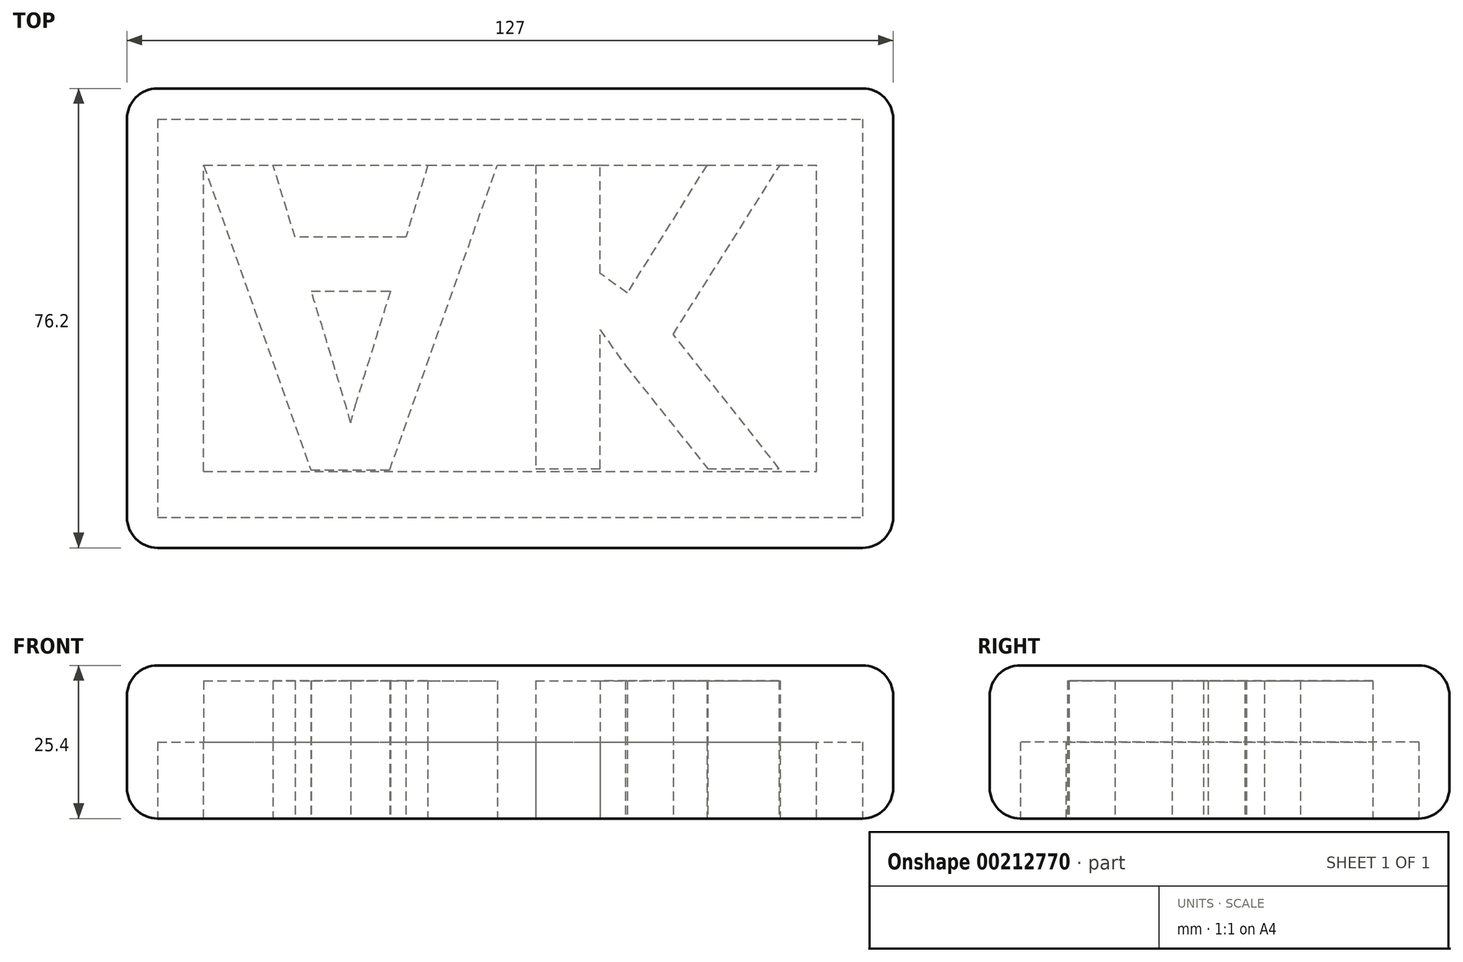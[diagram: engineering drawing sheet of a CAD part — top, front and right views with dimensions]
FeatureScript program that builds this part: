
annotation { "Feature Type Name" : "Feature", "Feature Type Description" : "" }
export const myFeature = defineFeature(function(context is Context, id is Id, definition is map)
    precondition{}
    {
        {
            var Q0;
            Q0=qCreatedBy(makeId("Top.planeOp"),FACE);
            var sketch = newSketch(context, id + "F0", { "sketchPlane" : qUnion([Q0])});
            skLineSegment(sketch, "E0.bottom", {"start": v(-63.5, 38.1) * mm, "end": v(63.5, 38.1) * mm});
            skLineSegment(sketch, "E0.top", {"start": v(-63.5, -38.1) * mm, "end": v(63.5, -38.1) * mm});
            skLineSegment(sketch, "E0.left", {"start": v(-63.5, 38.1) * mm, "end": v(-63.5, -38.1) * mm});
            skLineSegment(sketch, "E0.right", {"start": v(63.5, 38.1) * mm, "end": v(63.5, -38.1) * mm});
            skPoint(sketch, "E0.middle", {"position": v(0, 0) * mm});
            skSolve(sketch);
        }
        {
            var Q0;
            Q0=makeQuery(id+"F0.imprint","IMPRINT",FACE,{"disambiguationData":[TD([[makeQuery(id+"F0.imprint","IMPRINT",EDGE,{"derivedFrom":sQuery(id+"F0.wireOp",EDGE,"E0.bottom")}),-1.0]])]});
            extrude(context, id + "F1", {"entities" : qUnion([Q0]), "depth" : 25.4 * mm});
        }
        {
            var Q0;
            Q0=makeQuery(id+"F1.opExtrude","SWEPT_EDGE",EDGE,{"disambiguationData":[OSD([sQuery(id+"F0.wireOp",EDGE,"E0.bottom"),sQuery(id+"F0.wireOp",EDGE,"E0.left")])]});
            var Q1;
            Q1=makeQuery(id+"F1.opExtrude","CAP_EDGE",EDGE,{"disambiguationData":[OSD([sQuery(id+"F0.wireOp",EDGE,"E0.left")])],"isStart":false});
            var Q2;
            Q2=makeQuery(id+"F1.opExtrude","CAP_EDGE",EDGE,{"disambiguationData":[OSD([sQuery(id+"F0.wireOp",EDGE,"E0.bottom")])],"isStart":false});
            var Q3;
            Q3=makeQuery(id+"F1.opExtrude","CAP_EDGE",EDGE,{"disambiguationData":[OSD([sQuery(id+"F0.wireOp",EDGE,"E0.top")])],"isStart":false});
            var Q4;
            Q4=makeQuery(id+"F1.opExtrude","SWEPT_EDGE",EDGE,{"disambiguationData":[OSD([sQuery(id+"F0.wireOp",EDGE,"E0.top"),sQuery(id+"F0.wireOp",EDGE,"E0.left")])]});
            var Q5;
            Q5=makeQuery(id+"F1.opExtrude","CAP_EDGE",EDGE,{"disambiguationData":[OSD([sQuery(id+"F0.wireOp",EDGE,"E0.left")])],"isStart":true});
            var Q6;
            Q6=makeQuery(id+"F1.opExtrude","CAP_EDGE",EDGE,{"disambiguationData":[OSD([sQuery(id+"F0.wireOp",EDGE,"E0.bottom")])],"isStart":true});
            var Q7;
            Q7=makeQuery(id+"F1.opExtrude","SWEPT_EDGE",EDGE,{"disambiguationData":[OSD([sQuery(id+"F0.wireOp",EDGE,"E0.bottom"),sQuery(id+"F0.wireOp",EDGE,"E0.right")])]});
            var Q8;
            Q8=makeQuery(id+"F1.opExtrude","CAP_EDGE",EDGE,{"disambiguationData":[OSD([sQuery(id+"F0.wireOp",EDGE,"E0.right")])],"isStart":false});
            var Q9;
            Q9=makeQuery(id+"F1.opExtrude","CAP_EDGE",EDGE,{"disambiguationData":[OSD([sQuery(id+"F0.wireOp",EDGE,"E0.right")])],"isStart":true});
            var Q10;
            Q10=makeQuery(id+"F1.opExtrude","CAP_EDGE",EDGE,{"disambiguationData":[OSD([sQuery(id+"F0.wireOp",EDGE,"E0.top")])],"isStart":true});
            var Q11;
            Q11=makeQuery(id+"F1.opExtrude","SWEPT_EDGE",EDGE,{"disambiguationData":[OSD([sQuery(id+"F0.wireOp",EDGE,"E0.top"),sQuery(id+"F0.wireOp",EDGE,"E0.right")])]});
            fillet(context, id + "F2", {"entities" : qUnion([Q0, Q1, Q2, Q3, Q4, Q5, Q6, Q7, Q8, Q9, Q10, Q11]), "radius" : 5.08 * mm, "tangentPropagation" : true, "allowEdgeOverflow" : false});
        }
        {
            var Q0;
            Q0=makeQuery(id+"F1.opExtrude","CAP_FACE",FACE,{"disambiguationData":[OSD([sQuery(id+"F0.wireOp",EDGE,"E0.bottom"),sQuery(id+"F0.wireOp",EDGE,"E0.top"),sQuery(id+"F0.wireOp",EDGE,"E0.left"),sQuery(id+"F0.wireOp",EDGE,"E0.right")])],"isStart":true});
            extrude(context, id + "F3", {"entities" : qUnion([Q0]), "operationType" : NewBodyOperationType.REMOVE, "oppositeDirection" : true, "depth" : 12.7 * mm});
        }
        {
            var Q0;
            Q0=makeQuery(id+"F3.boolean.opBoolean","COPY",FACE,{"derivedFrom":makeQuery(id+"F3.opExtrude","CAP_FACE",FACE,{"disambiguationData":[OSD([sQuery(id+"F0.wireOp",EDGE,"E0.bottom"),sQuery(id+"F0.wireOp",EDGE,"E0.top"),sQuery(id+"F0.wireOp",EDGE,"E0.left"),sQuery(id+"F0.wireOp",EDGE,"E0.right")])],"isStart":false})});
            var sketch = newSketch(context, id + "F4", { "sketchPlane" : qUnion([Q0])});
            skLineSegment(sketch, "E1.bottom", {"start": v(-50.8, 25.4) * mm, "end": v(50.8, 25.4) * mm});
            skLineSegment(sketch, "E1.top", {"start": v(-50.8, -25.4) * mm, "end": v(50.8, -25.4) * mm});
            skLineSegment(sketch, "E1.left", {"start": v(-50.8, 25.4) * mm, "end": v(-50.8, -25.4) * mm});
            skLineSegment(sketch, "E1.right", {"start": v(50.8, 25.4) * mm, "end": v(50.8, -25.4) * mm});
            skPoint(sketch, "E1.middle", {"position": v(0, 0) * mm});
            skSolve(sketch);
        }
        {
            var Q0;
            Q0=makeQuery(id+"F4.imprint","IMPRINT",FACE,{"disambiguationData":[TD([[makeQuery(id+"F4.imprint","IMPRINT",EDGE,{"derivedFrom":sQuery(id+"F4.wireOp",EDGE,"E1.bottom")}),-1.0]])]});
            extrude(context, id + "F5", {"entities" : qUnion([Q0]), "operationType" : NewBodyOperationType.ADD, "depth" : 12.7 * mm});
        }
        {
            var Q0;
            Q0=makeQuery(id+"F5.opExtrude","CAP_FACE",FACE,{"disambiguationData":[OSD([sQuery(id+"F4.wireOp",EDGE,"E1.bottom"),sQuery(id+"F4.wireOp",EDGE,"E1.top"),sQuery(id+"F4.wireOp",EDGE,"E1.left"),sQuery(id+"F4.wireOp",EDGE,"E1.right")])],"isStart":false});
            var sketch = newSketch(context, id + "F6", { "sketchPlane" : qUnion([Q0])});
            skText(sketch, "E2", { "text": "AK", "fontName": "OpenSans-Bold.ttf"});
            const initialGuessF6  = {"E2": [-0.0508, -0.0254, 1, 0, 0.0508]};
            skSetInitialGuess(sketch, initialGuessF6);
            skSolve(sketch);
        }
        {
            var Q0;
            Q0 = qSketchRegion(id + "F6", true);
            extrude(context, id + "F7", {"entities" : qUnion([Q0]), "operationType" : NewBodyOperationType.REMOVE, "oppositeDirection" : true, "depth" : 22.86 * mm});
        }
    });
